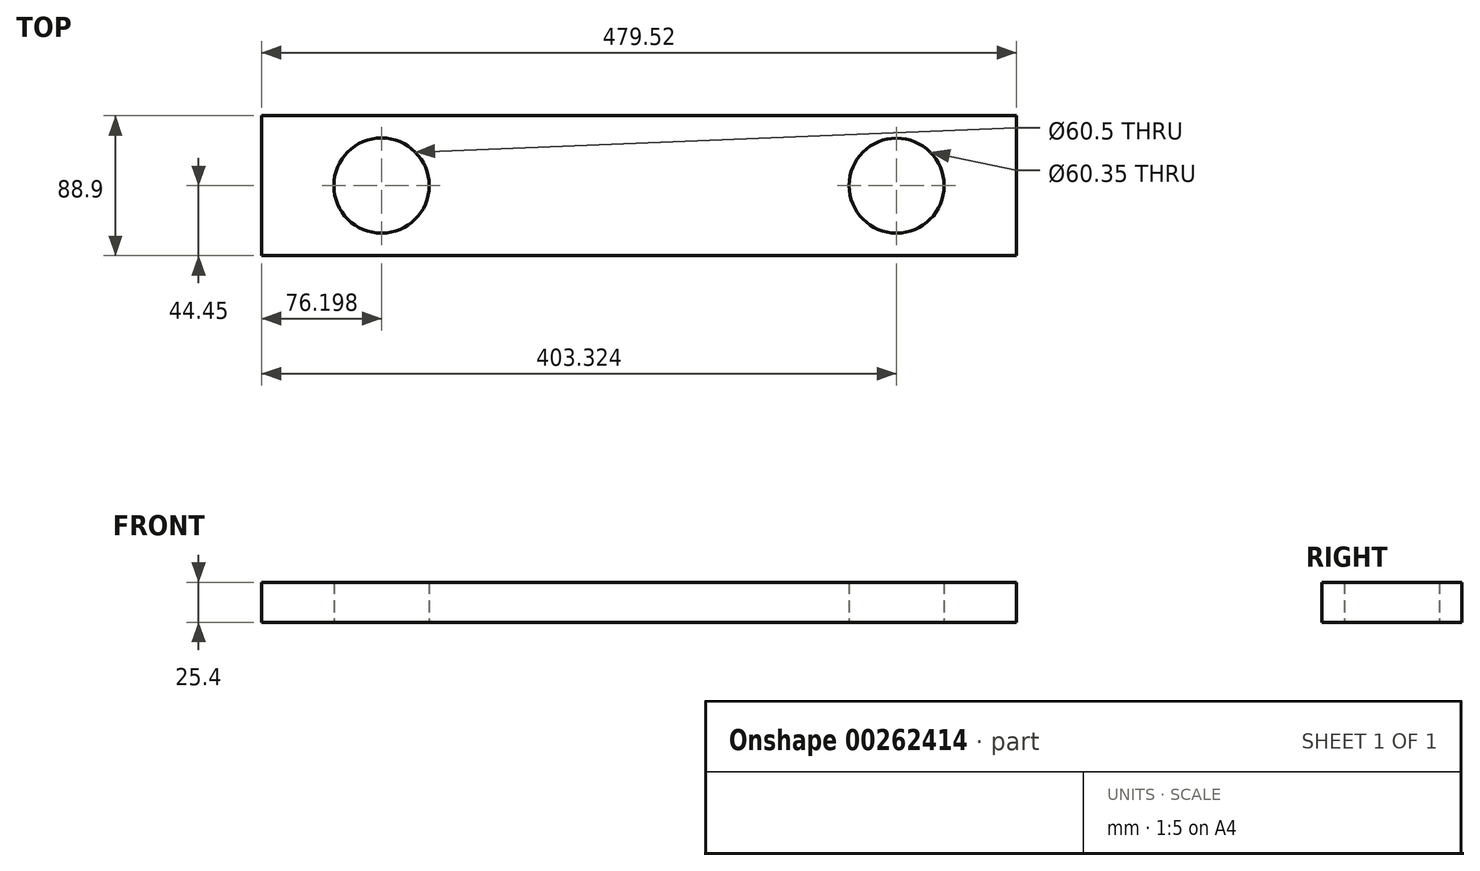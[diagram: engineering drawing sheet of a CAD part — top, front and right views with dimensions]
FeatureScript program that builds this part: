
annotation { "Feature Type Name" : "Feature", "Feature Type Description" : "" }
export const myFeature = defineFeature(function(context is Context, id is Id, definition is map)
    precondition{}
    {
        {
            var Q0;
            Q0=qCreatedBy(makeId("Top.planeOp"),FACE);
            var sketch = newSketch(context, id + "F0", { "sketchPlane" : qUnion([Q0])});
            skLineSegment(sketch, "E0", {"start": v(-136.02, 0) * mm, "end": v(130.68, 0) * mm});
            skCircle(sketch, "E1", {"center": v(-166.27, 0) * mm, "radius": 30.25 * mm});
            skCircle(sketch, "E2", {"center": v(160.85, 0) * mm, "radius": 30.18 * mm});
            skCircle(sketch, "E3", {"center": v(-166.27, 0) * mm, "radius": 44.45 * mm});
            skCircle(sketch, "E4", {"center": v(160.85, 0) * mm, "radius": 44.45 * mm});
            skLineSegment(sketch, "E5", {"start": v(-166.27, -44.45) * mm, "end": v(160.85, -44.45) * mm});
            skLineSegment(sketch, "E6", {"start": v(160.85, -44.45) * mm, "end": v(237.05, -44.45) * mm});
            skLineSegment(sketch, "E7", {"start": v(-166.27, -44.45) * mm, "end": v(-242.47, -44.45) * mm});
            skLineSegment(sketch, "E8", {"start": v(-166.27, 44.45) * mm, "end": v(-242.47, 44.45) * mm});
            skLineSegment(sketch, "E9", {"start": v(-242.47, 44.45) * mm, "end": v(-242.47, -44.45) * mm});
            skLineSegment(sketch, "E10", {"start": v(-166.27, 44.45) * mm, "end": v(160.85, 44.45) * mm});
            skLineSegment(sketch, "E11", {"start": v(160.85, 44.45) * mm, "end": v(237.05, 44.45) * mm});
            skLineSegment(sketch, "E12", {"start": v(237.05, 44.45) * mm, "end": v(237.05, -44.45) * mm});
            skSolve(sketch);
        }
        {
            var Q0;
            {var subQ5=sQuery(id+"F0.wireOp",EDGE,"E10");Q0=makeQuery(id+"F0.imprint","IMPRINT",FACE,{"disambiguationData":[TD([[makeQuery(id+"F0.imprint","IMPRINT",EDGE,{"derivedFrom":subQ5}),-1.0]])]});}
            var Q1;
            {var subQ0=sQuery(id+"F0.wireOp",EDGE,"E7");Q1=makeQuery(id+"F0.imprint","IMPRINT",FACE,{"disambiguationData":[TD([[makeQuery(id+"F0.imprint","IMPRINT",EDGE,{"derivedFrom":subQ0}),-1.0]])]});}
            var Q2;
            Q2=makeQuery(id+"F0.imprint","IMPRINT",FACE,{"disambiguationData":[TD([[makeQuery(id+"F0.imprint","IMPRINT",EDGE,{"derivedFrom":sQuery(id+"F0.wireOp",EDGE,"E1")}),-1.0]])]});
            var Q3;
            {var subQ5=sQuery(id+"F0.wireOp",EDGE,"E5");Q3=makeQuery(id+"F0.imprint","IMPRINT",FACE,{"disambiguationData":[TD([[makeQuery(id+"F0.imprint","IMPRINT",EDGE,{"derivedFrom":subQ5}),1.0]])]});}
            var Q4;
            Q4=makeQuery(id+"F0.imprint","IMPRINT",FACE,{"disambiguationData":[TD([[makeQuery(id+"F0.imprint","IMPRINT",EDGE,{"derivedFrom":sQuery(id+"F0.wireOp",EDGE,"E2")}),-1.0]])]});
            var Q5;
            {var subQ0=sQuery(id+"F0.wireOp",EDGE,"E6");Q5=makeQuery(id+"F0.imprint","IMPRINT",FACE,{"disambiguationData":[TD([[makeQuery(id+"F0.imprint","IMPRINT",EDGE,{"derivedFrom":subQ0}),1.0]])]});}
            extrude(context, id + "F1", {"entities" : qUnion([Q0, Q1, Q2, Q3, Q4, Q5]), "depth" : 25.4 * mm});
        }
    });
